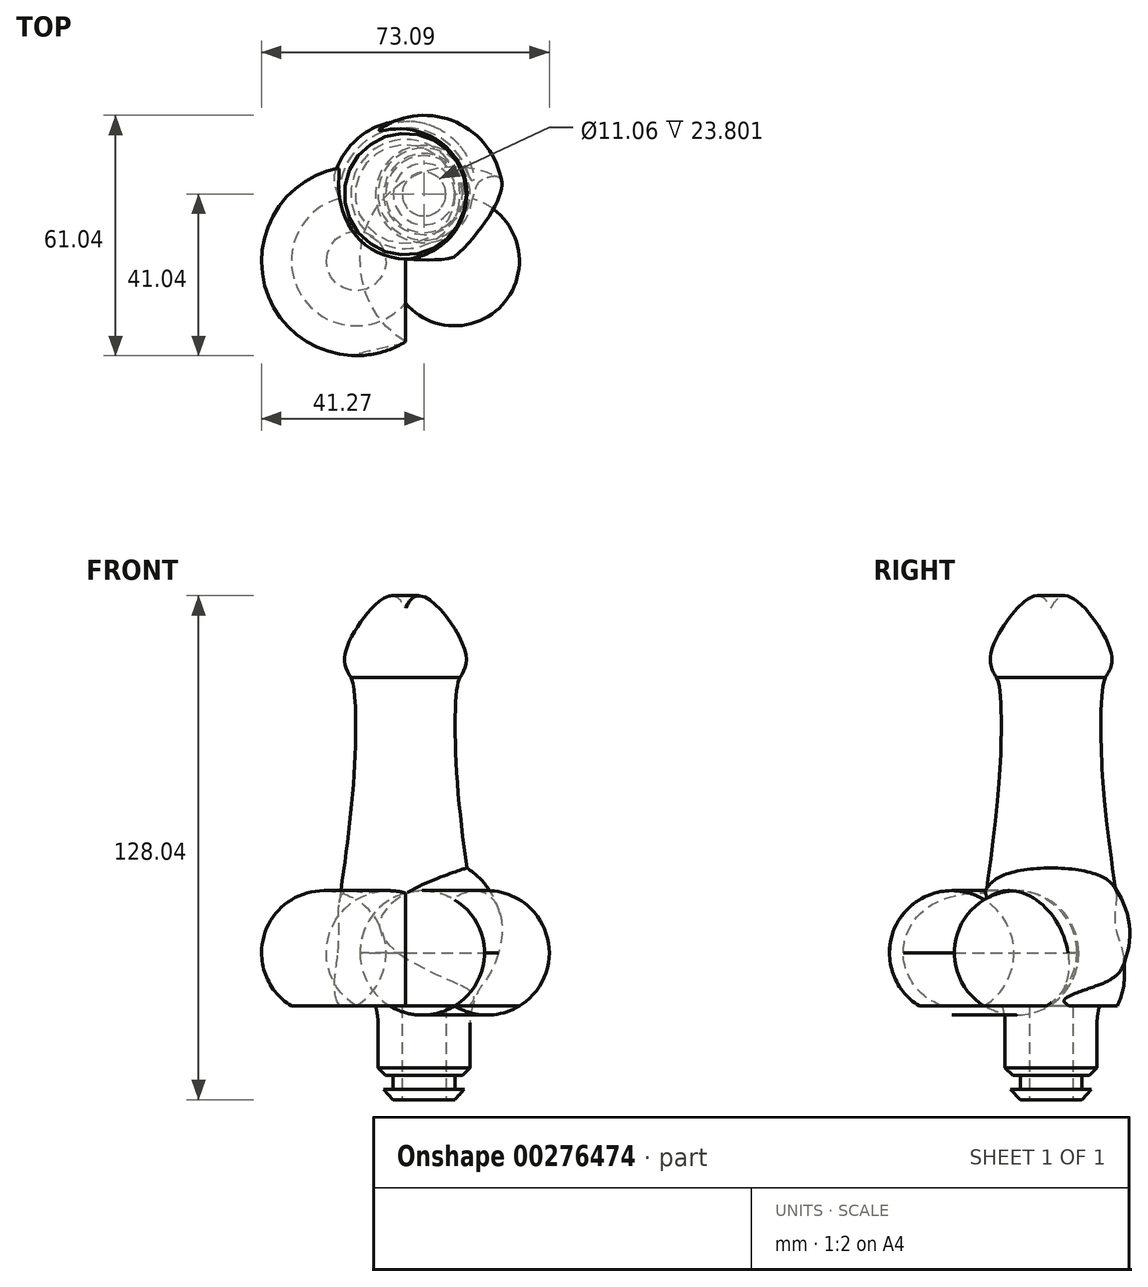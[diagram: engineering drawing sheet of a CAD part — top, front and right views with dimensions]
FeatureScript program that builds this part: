
annotation { "Feature Type Name" : "Feature", "Feature Type Description" : "" }
export const myFeature = defineFeature(function(context is Context, id is Id, definition is map)
    precondition{}
    {
        {
            var Q0;
            Q0=qCreatedBy(makeId("Front.planeOp"),FACE);
            var sketch = newSketch(context, id + "F0", { "sketchPlane" : qUnion([Q0])});
            skCircle(sketch, "E0", {"center": v(0, 0) * mm, "radius": 20 * mm});
            skLineSegment(sketch, "E1.bottom", {"start": v(11.7, -35.95) * mm, "end": v(-11.7, -35.95) * mm});
            skLineSegment(sketch, "E1.top", {"start": v(11.7, 12.66) * mm, "end": v(-11.7, 12.66) * mm});
            skLineSegment(sketch, "E1.left", {"start": v(11.7, -35.95) * mm, "end": v(11.7, 12.66) * mm});
            skLineSegment(sketch, "E1.right", {"start": v(-11.7, -35.95) * mm, "end": v(-11.7, 12.66) * mm});
            skPoint(sketch, "E1.middle", {"position": v(0, -11.65) * mm});
            skLineSegment(sketch, "E2", {"start": v(0, 20) * mm, "end": v(0, -35.95) * mm});
            skLineSegment(sketch, "E3", {"start": v(11.7, -34.06) * mm, "end": v(9.74, -35.95) * mm});
            skLineSegment(sketch, "E4", {"start": v(7.81, -35.95) * mm, "end": v(7.81, -39.42) * mm});
            skLineSegment(sketch, "E5", {"start": v(7.81, -39.42) * mm, "end": v(10.27, -39.42) * mm});
            skLineSegment(sketch, "E6", {"start": v(10.27, -39.42) * mm, "end": v(7.81, -42.1) * mm});
            skLineSegment(sketch, "E7", {"start": v(7.81, -42.1) * mm, "end": v(0, -42.1) * mm});
            skLineSegment(sketch, "E8", {"start": v(0, -42.1) * mm, "end": v(0, -35.95) * mm});
            skSolve(sketch);
        }
        {
            var Q0;
            {var subQ0=sQuery(id+"F0.wireOp",EDGE,"E2");var subQ1=sQuery(id+"F0.wireOp",EDGE,"E0");var subQ2=makeQuery(id+"F0.imprint","INTERSECT",VERTEX,{"disambiguationData":[OD(0.0)],"derivedFrom":[subQ1,subQ0]});Q0=makeQuery(id+"F0.imprint","IMPRINT",FACE,{"disambiguationData":[TD([[makeQuery(id+"F0.imprint","IMPRINT",EDGE,{"disambiguationData":[TD([[subQ2,1.0]])],"derivedFrom":subQ1}),1.0]])]});}
            var Q1;
            {var subQ0=sQuery(id+"F0.wireOp",EDGE,"E1.left");var subQ1=sQuery(id+"F0.wireOp",EDGE,"E0");var subQ2=makeQuery(id+"F0.imprint","INTERSECT",VERTEX,{"derivedFrom":[subQ1,subQ0]});Q1=makeQuery(id+"F0.imprint","IMPRINT",FACE,{"disambiguationData":[TD([[makeQuery(id+"F0.imprint","IMPRINT",EDGE,{"disambiguationData":[TD([[subQ2,1.0]])],"derivedFrom":subQ1}),1.0]])]});}
            var Q2;
            {var subQ0=sQuery(id+"F0.wireOp",EDGE,"E1.left");var subQ1=sQuery(id+"F0.wireOp",EDGE,"E0");var subQ2=makeQuery(id+"F0.imprint","INTERSECT",VERTEX,{"derivedFrom":[subQ1,subQ0]});Q2=makeQuery(id+"F0.imprint","IMPRINT",FACE,{"disambiguationData":[TD([[makeQuery(id+"F0.imprint","IMPRINT",EDGE,{"disambiguationData":[TD([[subQ2,1.0]])],"derivedFrom":subQ1}),-1.0]])]});}
            var Q3;
            {var subQ0=sQuery(id+"F0.wireOp",EDGE,"E4");Q3=makeQuery(id+"F0.imprint","IMPRINT",FACE,{"disambiguationData":[TD([[makeQuery(id+"F0.imprint","IMPRINT",EDGE,{"derivedFrom":subQ0}),-1.0]])]});}
            var Q4;
            Q4=sQuery(id+"F0.wireOp",EDGE,"E2");
            revolve(context, id + "F1", {"entities" : qUnion([Q0, Q1, Q2, Q3]), "axis" : qUnion([Q4]), "revolveType" : RevolveType.FULL});
        }
        {
            var Q0;
            Q0=makeQuery(id+"F1.opRevolve","SWEPT_EDGE",EDGE,{"disambiguationData":[OSD([sQuery(id+"F0.wireOp",EDGE,"E0"),sQuery(id+"F0.wireOp",EDGE,"E1.left")])]});
            fillet(context, id + "F2", {"entities" : qUnion([Q0]), "radius" : 15 * mm, "tangentPropagation" : true, "allowEdgeOverflow" : false});
        }
        {
            var Q0;
            Q0=makeQuery(id+"F1.opRevolve","SWEPT_FACE",FACE,{"disambiguationData":[OSD([sQuery(id+"F0.wireOp",EDGE,"E7")])]});
            var sketch = newSketch(context, id + "F3", { "sketchPlane" : qUnion([Q0])});
            skCircle(sketch, "E9", {"center": v(0, 0) * mm, "radius": 5.53 * mm});
            skSolve(sketch);
        }
        {
            var Q0;
            Q0 = qSketchRegion(id + "F3", true);
            extrude(context, id + "F4", {"entities" : qUnion([Q0]), "operationType" : NewBodyOperationType.REMOVE, "oppositeDirection" : true, "depth" : 47.3 * mm});
        }
        {
            var Q0;
            Q0=qCreatedBy(makeId("Front.planeOp"),FACE);
            var sketch = newSketch(context, id + "F5", { "sketchPlane" : qUnion([Q0])});
            skLineSegment(sketch, "E10", {"start": v(-21.53, -18.3) * mm, "end": v(12.09, -18.3) * mm});
            skFitSpline(sketch, "E11", {"points": [v(12.09, -18.3) * mm, v(13.89, -11.4) * mm, v(8.76, 34.94) * mm, v(9.14, 65.14) * mm, v(9.9, 65.33) * mm], "startDerivative": vector(14.66, 31.21) * mm, "endDerivative": vector(14.2, -2.24) * mm});
            skLineSegment(sketch, "E12", {"start": v(-4.72, -18.3) * mm, "end": v(-4.72, 65.14) * mm});
            skFitSpline(sketch, "E13", {"points": [v(9.14, 65.14) * mm, v(10.39, 72) * mm, v(-1.7, 85.9) * mm, v(-4.72, 82.82) * mm, v(-4.72, 82.95) * mm], "startDerivative": vector(11.6, 19.08) * mm, "endDerivative": vector(0.78, 5.53) * mm});
            skLineSegment(sketch, "E14", {"start": v(-4.72, 82.82) * mm, "end": v(-4.72, 65.14) * mm});
            skSolve(sketch);
        }
        {
            var Q0;
            {var subQ4=sQuery(id+"F5.wireOp",EDGE,"E12");Q0=makeQuery(id+"F5.imprint","IMPRINT",FACE,{"disambiguationData":[TD([[makeQuery(id+"F5.imprint","IMPRINT",EDGE,{"derivedFrom":subQ4}),-1.0]])]});}
            var Q1;
            Q1=sQuery(id+"F5.wireOp",EDGE,"E14");
            revolve(context, id + "F6", {"entities" : qUnion([Q0]), "axis" : qUnion([Q1]), "revolveType" : RevolveType.FULL});
        }
        {
            var Q0;
            Q0=qCreatedBy(makeId("Front.planeOp"),FACE);
            var sketch = newSketch(context, id + "F7", { "sketchPlane" : qUnion([Q0])});
            skLineSegment(sketch, "E15.0", {"start": v(-4.72, -18.3) * mm, "end": v(-4.72, 65.14) * mm});
            skLineSegment(sketch, "E16.0", {"start": v(-21.53, -18.3) * mm, "end": v(12.09, -18.3) * mm});
            skLineSegment(sketch, "E17", {"start": v(12.09, -18.3) * mm, "end": v(22.07, -18.3) * mm});
            skLineSegment(sketch, "E18", {"start": v(7.78, -18.3) * mm, "end": v(7.78, -3.5) * mm});
            skArc(sketch, "E19", {"start": v(7.78, -18.3) * mm, "mid": v(31.82, -4.8) * mm, "end": v(7.78, 8.7) * mm});
            skLineSegment(sketch, "E20", {"start": v(7.78, -3.5) * mm, "end": v(7.78, 8.7) * mm});
            skSolve(sketch);
        }
        {
            var Q0;
            Q0=sQuery(id+"F5.wireOp",EDGE,"E10");
            cPoint(context, id + "F8", {"entities" : qUnion([Q0]), "parameter" : 0.5});
        }
        {
            var Q0;
            Q0=qCreatedBy(makeId("Right.planeOp"),FACE);
            var Q1;
            Q1 = qCreatedBy(id + "F8" ,VERTEX);
            cPlane(context, id + "F9", {"entities" : qUnion([Q0, Q1]), "cplaneType" : CPlaneType.PLANE_POINT, "offset" : 25 * mm, "width" : 150 * mm, "height" : 150 * mm});
        }
        {
            var Q0;
            Q0=qCreatedBy(makeId("Front.planeOp"),FACE);
            cPlane(context, id + "F10", {"entities" : qUnion([Q0]), "cplaneType" : CPlaneType.OFFSET, "offset" : 17 * mm, "width" : 150 * mm, "height" : 150 * mm});
        }
        {
            var Q0;
            Q0=qCreatedBy(id+"F10.planeOp",FACE);
            var sketch = newSketch(context, id + "F11", { "sketchPlane" : qUnion([Q0])});
            skArc(sketch, "E21.0", {"start": v(7.78, -18.3) * mm, "mid": v(31.82, -4.8) * mm, "end": v(7.78, 8.7) * mm});
            skLineSegment(sketch, "E22.0", {"start": v(7.78, -3.5) * mm, "end": v(7.78, 8.7) * mm});
            skLineSegment(sketch, "E23.0", {"start": v(7.78, -18.3) * mm, "end": v(7.78, -3.5) * mm});
            skPoint(sketch, "E24.0", {"position": v(17.08, -18.3) * mm});
            skLineSegment(sketch, "E25.0", {"start": v(-21.53, -18.3) * mm, "end": v(12.09, -18.3) * mm});
            skLineSegment(sketch, "E26.0", {"start": v(12.09, -18.3) * mm, "end": v(22.07, -18.3) * mm});
            skLineSegment(sketch, "E27", {"start": v(22.07, -18.3) * mm, "end": v(24.24, -18.3) * mm});
            skSolve(sketch);
        }
        {
            var Q0;
            {var subQ4=sQuery(id+"F11.wireOp",EDGE,"E22.0");Q0=makeQuery(id+"F11.imprint","IMPRINT",FACE,{"disambiguationData":[TD([[makeQuery(id+"F11.imprint","IMPRINT",EDGE,{"derivedFrom":subQ4}),-1.0]])]});}
            var Q1;
            Q1=sQuery(id+"F11.wireOp",EDGE,"E22.0");
            revolve(context, id + "F12", {"entities" : qUnion([Q0]), "axis" : qUnion([Q1]), "revolveType" : RevolveType.FULL});
        }
        {
            var Q0;
            Q0=makeQuery(id+"F12.opRevolve","SWEPT_BODY",BODY,{"disambiguationData":[OSD([sQuery(id+"F11.wireOp",EDGE,"E21.0"),sQuery(id+"F11.wireOp",EDGE,"E22.0"),sQuery(id+"F11.wireOp",EDGE,"E23.0"),sQuery(id+"F11.wireOp",EDGE,"E25.0"),sQuery(id+"F11.wireOp",EDGE,"E26.0"),sQuery(id+"F11.wireOp",EDGE,"E27")])]});
            var Q1;
            Q1=qCreatedBy(id+"F9.planeOp",FACE);
            mirror(context, id + "F13", {"operationType" : NewBodyOperationType.ADD, "entities" : qUnion([Q0]), "mirrorPlane" : qUnion([Q1])});
        }
    });
